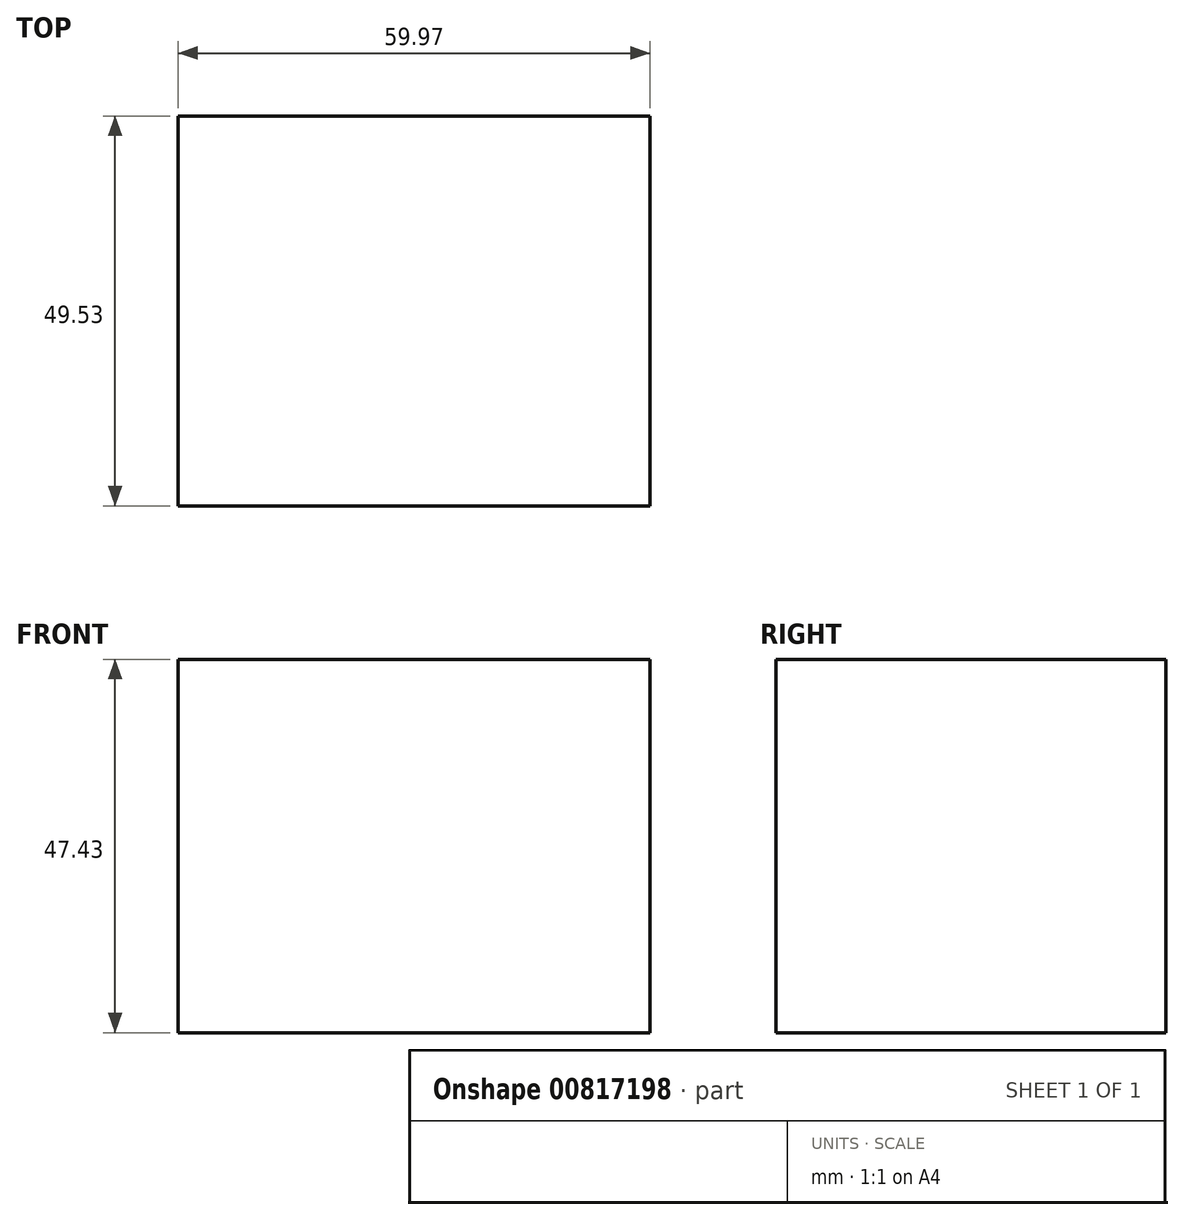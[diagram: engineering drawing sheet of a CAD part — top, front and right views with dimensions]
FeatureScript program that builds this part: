
annotation { "Feature Type Name" : "Feature", "Feature Type Description" : "" }
export const myFeature = defineFeature(function(context is Context, id is Id, definition is map)
    precondition{}
    {
        {
            var Q0;
            Q0=qCreatedBy(makeId("Front.planeOp"),FACE);
            var sketch = newSketch(context, id + "F0", { "sketchPlane" : qUnion([Q0])});
            skLineSegment(sketch, "E0.bottom", {"start": v(-24.36, 12.9) * mm, "end": v(35.6, 12.9) * mm});
            skLineSegment(sketch, "E0.top", {"start": v(-24.36, -34.53) * mm, "end": v(35.6, -34.53) * mm});
            skLineSegment(sketch, "E0.left", {"start": v(-24.36, 12.9) * mm, "end": v(-24.36, -34.53) * mm});
            skLineSegment(sketch, "E0.right", {"start": v(35.6, 12.9) * mm, "end": v(35.6, -34.53) * mm});
            skSolve(sketch);
        }
        {
            var Q0;
            Q0 = qSketchRegion(id + "F0", true);
            extrude(context, id + "F1", {"entities" : qUnion([Q0]), "depth" : 49.53 * mm, "offsetDistance" : 25.4 * mm});
        }
    });
